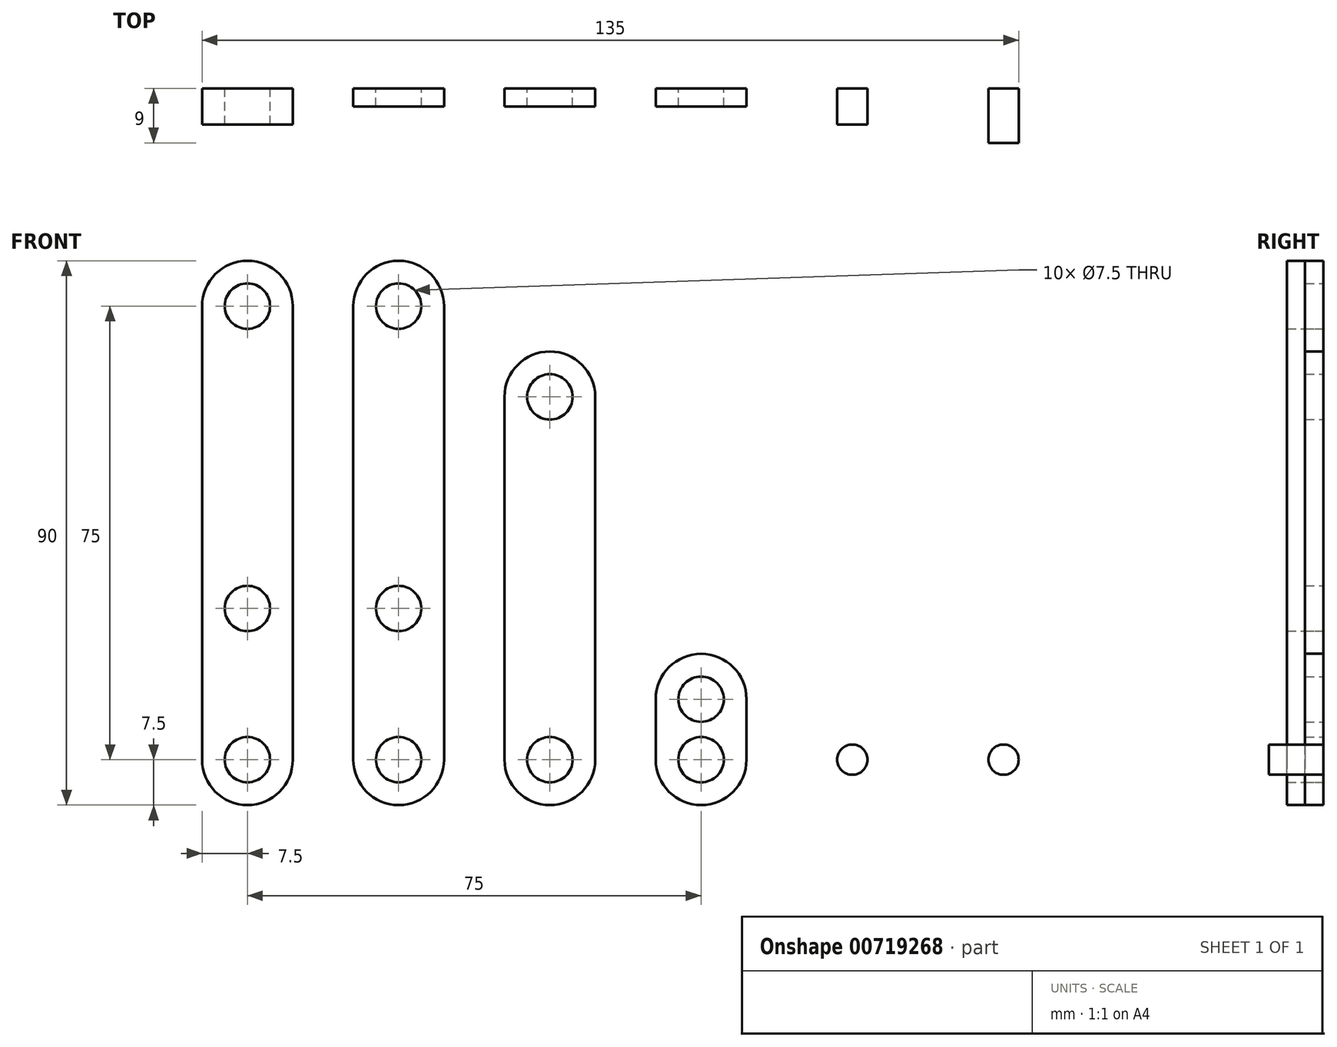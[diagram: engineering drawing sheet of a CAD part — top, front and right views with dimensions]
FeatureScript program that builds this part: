
annotation { "Feature Type Name" : "Feature", "Feature Type Description" : "" }
export const myFeature = defineFeature(function(context is Context, id is Id, definition is map)
    precondition{}
    {
        {
            assignVariable(context, id + "F0", {"name" : "thinkness", "anyValue" : 3});
        }
        {
            var Q0;
            Q0=qCreatedBy(makeId("Front.planeOp"),FACE);
            var sketch = newSketch(context, id + "F1", { "sketchPlane" : qUnion([Q0])});
            skArc(sketch, "E0", {"start": v(-32.5, 0) * mm, "mid": v(-25, -7.5) * mm, "end": v(-17.5, 0) * mm});
            skCircle(sketch, "E1", {"center": v(-25, 10) * mm, "radius": 3.75 * mm});
            skCircle(sketch, "E2", {"center": v(-25, 0) * mm, "radius": 3.75 * mm});
            skLineSegment(sketch, "E3", {"start": v(-32.5, 10) * mm, "end": v(-32.5, 0) * mm});
            skLineSegment(sketch, "E4", {"start": v(-17.5, 10) * mm, "end": v(-17.5, 0) * mm});
            skArc(sketch, "E5.trimOffspring", {"start": v(-17.5, 10) * mm, "mid": v(-25, 17.5) * mm, "end": v(-32.5, 10) * mm});
            skArc(sketch, "E6", {"start": v(-57.5, 0) * mm, "mid": v(-50, -7.5) * mm, "end": v(-42.5, 0) * mm});
            skCircle(sketch, "E7", {"center": v(-50, 60) * mm, "radius": 3.75 * mm});
            skCircle(sketch, "E8", {"center": v(-50, 0) * mm, "radius": 3.75 * mm});
            skLineSegment(sketch, "E9", {"start": v(-57.5, 60) * mm, "end": v(-57.5, 0) * mm});
            skLineSegment(sketch, "E10", {"start": v(-42.5, 60) * mm, "end": v(-42.5, 0) * mm});
            skArc(sketch, "E11.trimOffspring", {"start": v(-42.5, 60) * mm, "mid": v(-50, 67.5) * mm, "end": v(-57.5, 60) * mm});
            skArc(sketch, "E12", {"start": v(-82.5, 0) * mm, "mid": v(-75, -7.5) * mm, "end": v(-67.5, 0) * mm});
            skCircle(sketch, "E13", {"center": v(-75, 75) * mm, "radius": 3.75 * mm});
            skCircle(sketch, "E14", {"center": v(-75, 0) * mm, "radius": 3.75 * mm});
            skLineSegment(sketch, "E15", {"start": v(-82.5, 75) * mm, "end": v(-82.5, 0) * mm});
            skLineSegment(sketch, "E16", {"start": v(-67.5, 75) * mm, "end": v(-67.5, 0) * mm});
            skArc(sketch, "E17.trimOffspring", {"start": v(-67.5, 75) * mm, "mid": v(-75, 82.5) * mm, "end": v(-82.5, 75) * mm});
            skCircle(sketch, "E18", {"center": v(-75, 25) * mm, "radius": 3.75 * mm});
            skArc(sketch, "E19", {"start": v(-107.5, 0) * mm, "mid": v(-100, -7.5) * mm, "end": v(-92.5, 0) * mm});
            skCircle(sketch, "E20", {"center": v(-100, 75) * mm, "radius": 3.75 * mm});
            skCircle(sketch, "E21", {"center": v(-100, 0) * mm, "radius": 3.75 * mm});
            skLineSegment(sketch, "E22", {"start": v(-107.5, 75) * mm, "end": v(-107.5, 0) * mm});
            skLineSegment(sketch, "E23", {"start": v(-92.5, 75) * mm, "end": v(-92.5, 0) * mm});
            skArc(sketch, "E24.trimOffspring", {"start": v(-92.5, 75) * mm, "mid": v(-100, 82.5) * mm, "end": v(-107.5, 75) * mm});
            skCircle(sketch, "E25", {"center": v(-100, 25) * mm, "radius": 3.75 * mm});
            skSolve(sketch);
        }
        {
            var Q0;
            Q0=makeQuery(id+"F1.imprint","IMPRINT",FACE,{"disambiguationData":[TD([[makeQuery(id+"F1.imprint","IMPRINT",EDGE,{"derivedFrom":sQuery(id+"F1.wireOp",EDGE,"E0")}),1.0]])]});
            var Q1;
            Q1=makeQuery(id+"F1.imprint","IMPRINT",FACE,{"disambiguationData":[TD([[makeQuery(id+"F1.imprint","IMPRINT",EDGE,{"derivedFrom":sQuery(id+"F1.wireOp",EDGE,"E6")}),1.0]])]});
            var Q2;
            Q2=makeQuery(id+"F1.imprint","IMPRINT",FACE,{"disambiguationData":[TD([[makeQuery(id+"F1.imprint","IMPRINT",EDGE,{"derivedFrom":sQuery(id+"F1.wireOp",EDGE,"E12")}),1.0]])]});
            extrude(context, id + "F2", {"entities" : qUnion([Q0, Q1, Q2]), "depth" : (getVariable(context, 'thinkness')) * mm, "offsetDistance" : 25 * mm});
        }
        {
            var Q0;
            Q0=qCreatedBy(makeId("Front.planeOp"),FACE);
            var sketch = newSketch(context, id + "F3", { "sketchPlane" : qUnion([Q0])});
            skCircle(sketch, "E26", {"center": v(0, 0) * mm, "radius": 2.5 * mm});
            skCircle(sketch, "E27", {"center": v(25, 0) * mm, "radius": 2.5 * mm});
            skSolve(sketch);
        }
        {
            var Q0;
            Q0=makeQuery(id+"F3.imprint","IMPRINT",FACE,{"disambiguationData":[TD([[makeQuery(id+"F3.imprint","IMPRINT",EDGE,{"derivedFrom":sQuery(id+"F3.wireOp",EDGE,"E26")}),1.0]])]});
            extrude(context, id + "F4", {"entities" : qUnion([Q0]), "depth" : (getVariable(context, 'thinkness') * 2) * mm, "offsetDistance" : 25 * mm});
        }
        {
            var Q0;
            Q0=makeQuery(id+"F3.imprint","IMPRINT",FACE,{"disambiguationData":[TD([[makeQuery(id+"F3.imprint","IMPRINT",EDGE,{"derivedFrom":sQuery(id+"F3.wireOp",EDGE,"E27")}),1.0]])]});
            extrude(context, id + "F5", {"entities" : qUnion([Q0]), "depth" : (getVariable(context, 'thinkness') * 3) * mm, "offsetDistance" : 25 * mm});
        }
        {
            var Q0;
            Q0=makeQuery(id+"F1.imprint","IMPRINT",FACE,{"disambiguationData":[TD([[makeQuery(id+"F1.imprint","IMPRINT",EDGE,{"derivedFrom":sQuery(id+"F1.wireOp",EDGE,"E19")}),1.0]])]});
            extrude(context, id + "F6", {"entities" : qUnion([Q0]), "depth" : (getVariable(context, 'thinkness') * 2) * mm, "offsetDistance" : 25 * mm});
        }
    });
